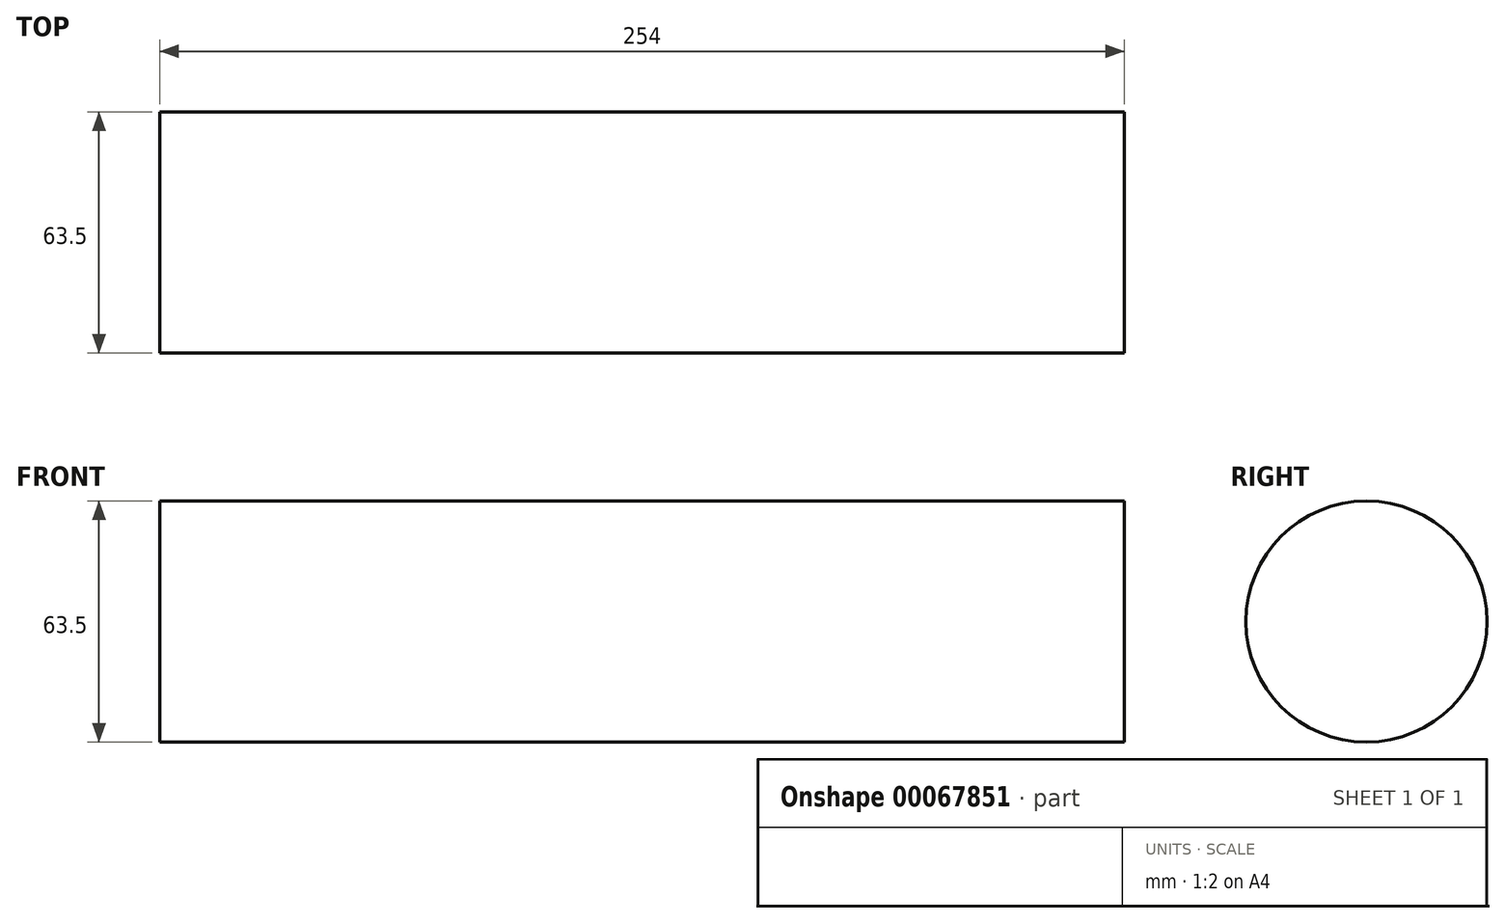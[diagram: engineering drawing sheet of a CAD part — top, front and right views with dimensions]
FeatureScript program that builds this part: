
annotation { "Feature Type Name" : "Feature", "Feature Type Description" : "" }
export const myFeature = defineFeature(function(context is Context, id is Id, definition is map)
    precondition{}
    {
        {
            var Q0;
            Q0=qCreatedBy(makeId("Right.planeOp"),FACE);
            var sketch = newSketch(context, id + "F0", { "sketchPlane" : qUnion([Q0])});
            skCircle(sketch, "E0", {"center": v(0, 0) * mm, "radius": 31.75 * mm});
            skSolve(sketch);
        }
        {
            var Q0;
            Q0=makeQuery(id+"F0.imprint","IMPRINT",FACE,{"disambiguationData":[TD([[makeQuery(id+"F0.imprint","IMPRINT",EDGE,{"derivedFrom":sQuery(id+"F0.wireOp",EDGE,"E0")}),1.0]])]});
            extrude(context, id + "F1", {"entities" : qUnion([Q0]), "depth" : 254 * mm});
        }
    });
